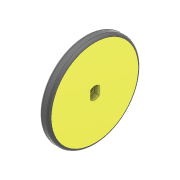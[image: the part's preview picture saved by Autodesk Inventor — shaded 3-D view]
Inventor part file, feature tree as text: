
AUTODESK INVENTOR PART (.ipt)
format: ipt  version: 2022 (Build 260153000, 153)  size: 129,024 bytes
history: native  units: mm
features: sketch x3, extrude x2, hole x1, fillet x1
ambient origin geometry x8: Origin, YZ Plane, XZ Plane, XY Plane, X Axis, Y Axis, Z Axis, Center Point
bodies: Solid1 (feature_tree)
feature tree (7):
  extrude  "Extrusion1"  Depth=4.0mm
  extrude  "Extrusion2"  Depth=3.5mm
  hole  "Hole1"  [1 undecoded]
  fillet  "Fillet1"  [1 undecoded]
  sketch  "Sketch1"  dims[d1=4.0mm d2=0.0mm d3=38.0mm]
  sketch  "Sketch2"  dims[d5=3.5mm d6=5.0mm]
  sketch  "Sketch3"  dims[d7=2.0mm d8=0.0mm d9=2.0mm d10=6.0mm d11=4.0mm d12=2.0mm d13=90.0deg d14=8.0mm d15=20.594885mm d16=1.0mm]
note: 2 required parameter values undecoded (feature->parameter linkage not recoverable at this tier; creation-order binding heuristic only, values carry confidence <= 0.55)
